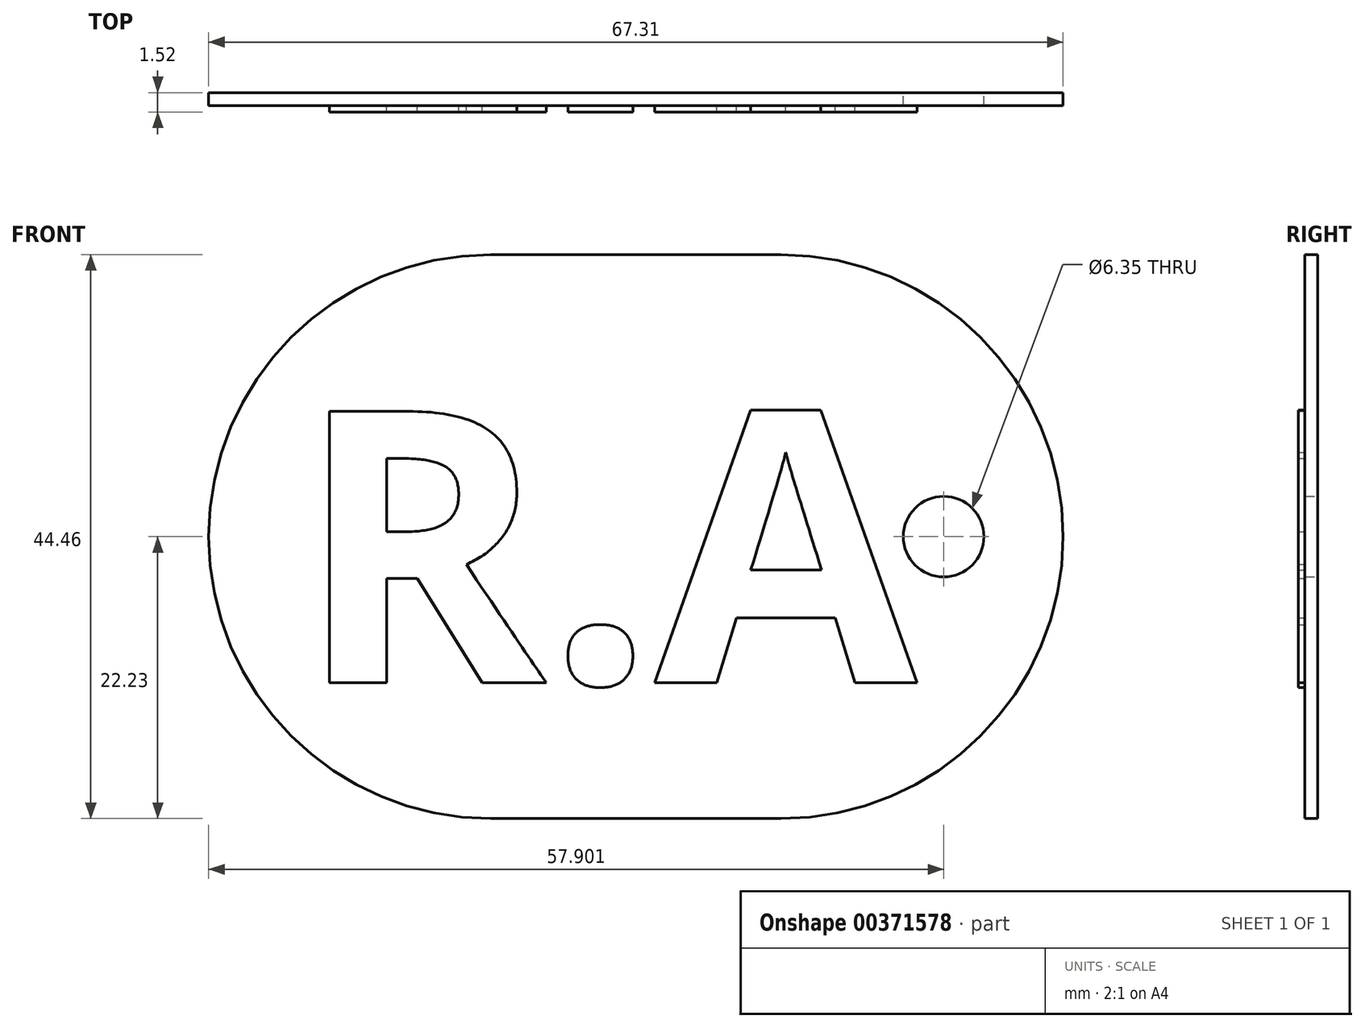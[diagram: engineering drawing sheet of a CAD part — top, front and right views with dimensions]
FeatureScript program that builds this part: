
annotation { "Feature Type Name" : "Feature", "Feature Type Description" : "" }
export const myFeature = defineFeature(function(context is Context, id is Id, definition is map)
    precondition{}
    {
        {
            var Q0;
            Q0=qCreatedBy(makeId("Front.planeOp"),FACE);
            var sketch = newSketch(context, id + "F0", { "sketchPlane" : qUnion([Q0])});
            skArc(sketch, "E0", {"start": v(-52.79, 22.23) * mm, "mid": v(-75.01, 0) * mm, "end": v(-52.79, -22.23) * mm});
            skArc(sketch, "E1", {"start": v(-29.93, -22.23) * mm, "mid": v(-7.7, 0) * mm, "end": v(-29.93, 22.23) * mm});
            skLineSegment(sketch, "E2", {"start": v(-52.79, 22.23) * mm, "end": v(-29.93, 22.23) * mm});
            skLineSegment(sketch, "E3", {"start": v(-52.79, -22.23) * mm, "end": v(-29.93, -22.23) * mm});
            skCircle(sketch, "E4", {"center": v(-17.1, 0) * mm, "radius": 3.18 * mm});
            skPoint(sketch, "E4.centerSnap0", {"position": v(-7.7, 0) * mm});
            skSolve(sketch);
        }
        {
            var Q0;
            Q0=makeQuery(id+"F0.imprint","IMPRINT",FACE,{"disambiguationData":[TD([[makeQuery(id+"F0.imprint","IMPRINT",EDGE,{"derivedFrom":sQuery(id+"F0.wireOp",EDGE,"E0")}),1.0]])]});
            extrude(context, id + "F1", {"entities" : qUnion([Q0]), "depth" : 1.02 * mm});
        }
        {
            var Q0;
            Q0=qCreatedBy(makeId("Front.planeOp"),FACE);
            var sketch = newSketch(context, id + "F2", { "sketchPlane" : qUnion([Q0])});
            skText(sketch, "E5", { "text": "R.A", "fontName": "OpenSans-Bold.ttf"});
            const initialGuessF2  = {"E5": [-0.0682, -0.01151, 1, 0, 0.02157]};
            skSetInitialGuess(sketch, initialGuessF2);
            skSolve(sketch);
        }
        {
            var Q0;
            Q0 = qSketchRegion(id + "F2", true);
            extrude(context, id + "F3", {"entities" : qUnion([Q0]), "operationType" : NewBodyOperationType.ADD, "depth" : 1.52 * mm});
        }
    });
